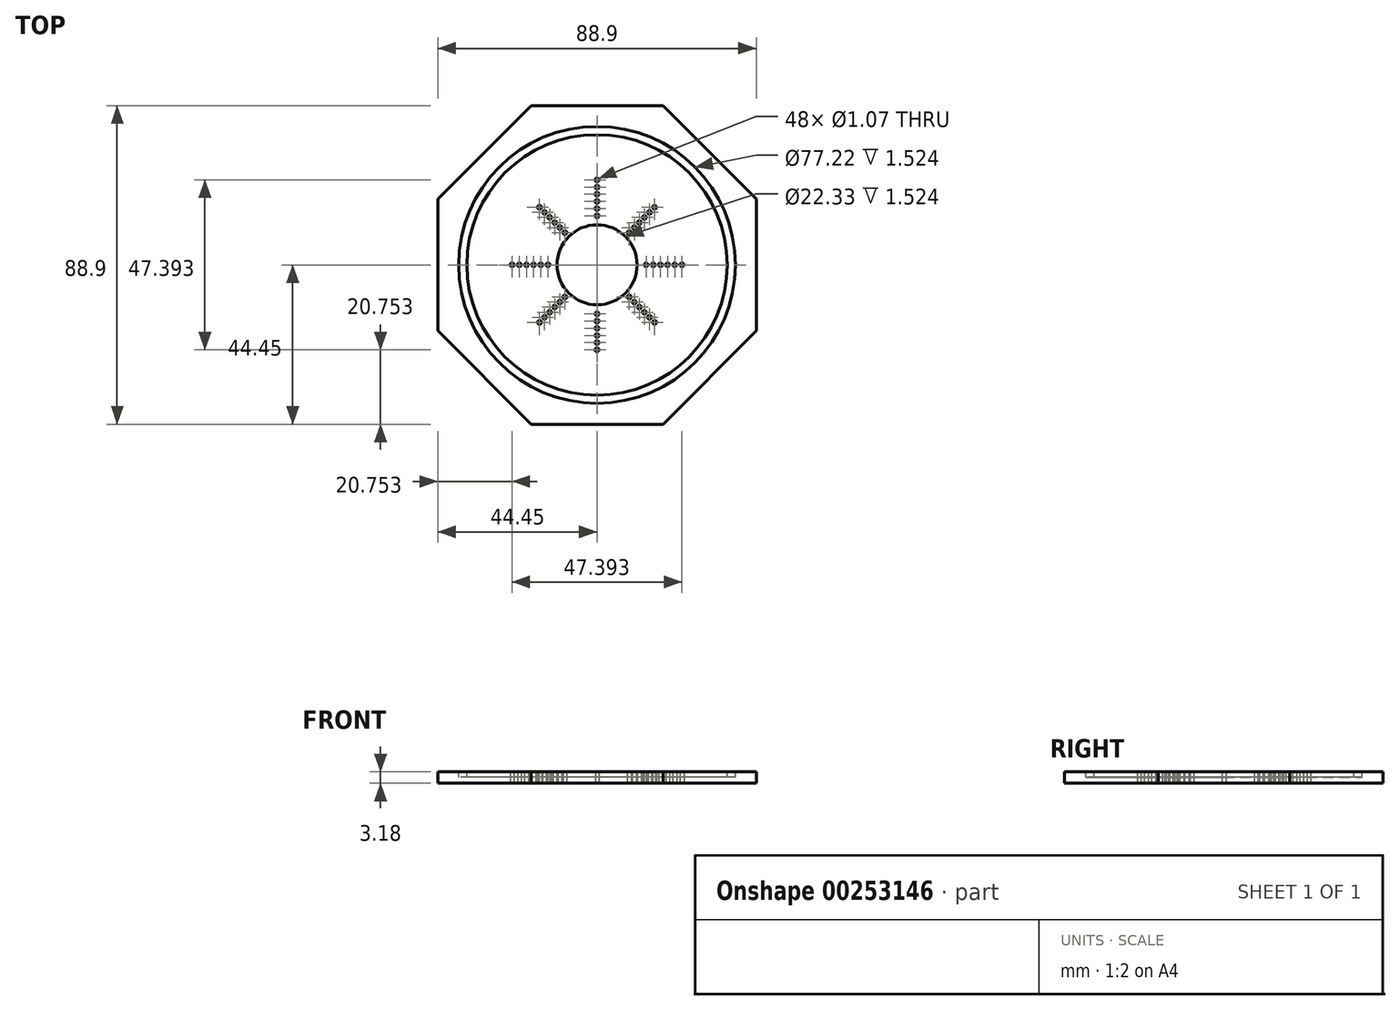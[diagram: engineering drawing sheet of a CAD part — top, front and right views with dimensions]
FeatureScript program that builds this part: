
annotation { "Feature Type Name" : "Feature", "Feature Type Description" : "" }
export const myFeature = defineFeature(function(context is Context, id is Id, definition is map)
    precondition{}
    {
        {
            var Q0;
            Q0=qCreatedBy(makeId("Top.planeOp"),FACE);
            var sketch = newSketch(context, id + "F0", { "sketchPlane" : qUnion([Q0])});
            skCircle(sketch, "E0", {"center": v(0, 0) * mm, "radius": 44.45 * mm, "construction": true});
            skLineSegment(sketch, "E1.bottom", {"start": v(-18.41, 44.45) * mm, "end": v(18.41, 44.45) * mm});
            skLineSegment(sketch, "E1.top", {"start": v(-18.41, -44.45) * mm, "end": v(18.41, -44.45) * mm});
            skLineSegment(sketch, "E1.left", {"start": v(-44.45, 18.41) * mm, "end": v(-44.45, -18.41) * mm});
            skLineSegment(sketch, "E1.right", {"start": v(44.45, 18.41) * mm, "end": v(44.45, -18.41) * mm});
            skLineSegment(sketch, "E2", {"start": v(-44.45, 18.41) * mm, "end": v(-18.41, 44.45) * mm});
            skLineSegment(sketch, "E3", {"start": v(0, 44.45) * mm, "end": v(0, -44.45) * mm, "construction": true});
            skLineSegment(sketch, "E4.MirrorCS", {"start": v(44.45, 18.41) * mm, "end": v(18.41, 44.45) * mm});
            skLineSegment(sketch, "E5", {"start": v(-44.45, 0) * mm, "end": v(44.45, 0) * mm});
            skLineSegment(sketch, "E6.MirrorCS", {"start": v(-44.45, -18.41) * mm, "end": v(-18.41, -44.45) * mm});
            skLineSegment(sketch, "E7.MirrorCS", {"start": v(44.45, -18.41) * mm, "end": v(18.41, -44.45) * mm});
            skPoint(sketch, "E8.orphan", {"position": v(-44.45, 44.45) * mm});
            skPoint(sketch, "E9.orphan", {"position": v(44.45, 44.45) * mm});
            skPoint(sketch, "E10.orphan", {"position": v(44.45, -44.45) * mm});
            skPoint(sketch, "E11.orphan", {"position": v(-44.45, -44.45) * mm});
            skSolve(sketch);
        }
        {
            var Q0;
            Q0=qSketchRegion(id+"F0",true);
            extrude(context, id + "F1", {"entities" : qUnion([Q0]), "depth" : 3.17 * mm});
        }
        {
            var Q0;
            Q0=makeQuery(id+"F1.opExtrude","CAP_FACE",FACE,{"disambiguationData":[OSD([sQuery(id+"F0.wireOp",EDGE,"E1.bottom"),sQuery(id+"F0.wireOp",EDGE,"E1.top"),sQuery(id+"F0.wireOp",EDGE,"E1.left"),sQuery(id+"F0.wireOp",EDGE,"E1.right")])],"isStart":false});
            var sketch = newSketch(context, id + "F2", { "sketchPlane" : qUnion([Q0])});
            skCircle(sketch, "E12", {"center": v(0, 0) * mm, "radius": 38.6 * mm});
            skCircle(sketch, "E13", {"center": v(0, 0) * mm, "radius": 36.32 * mm});
            skCircle(sketch, "E14", {"center": v(0, 0) * mm, "radius": 11.16 * mm});
            skSolve(sketch);
        }
        {
            var Q0;
            Q0=qSketchRegion(id+"F2",true);
            var Q1;
            Q1=makeQuery(id+"F2.imprint","IMPRINT",FACE,{"disambiguationData":[TD([[makeQuery(id+"F2.imprint","IMPRINT",EDGE,{"derivedFrom":sQuery(id+"F2.wireOp",EDGE,"E14")}),1.0]])]});
            extrude(context, id + "F3", {"entities" : qUnion([Q0, Q1]), "operationType" : NewBodyOperationType.REMOVE, "oppositeDirection" : true, "depth" : 1.52 * mm});
        }
        {
            var Q0;
            Q0=qCreatedBy(makeId("Top.planeOp"),FACE);
            var sketch = newSketch(context, id + "F4", { "sketchPlane" : qUnion([Q0])});
            skCircle(sketch, "E15", {"center": v(0, -13.7) * mm, "radius": 0.53 * mm});
            skCircle(sketch, "E16", {"center": v(0, -15.7) * mm, "radius": 0.53 * mm});
            skCircle(sketch, "E17", {"center": v(0, -17.7) * mm, "radius": 0.53 * mm});
            skCircle(sketch, "E18", {"center": v(0, -19.7) * mm, "radius": 0.53 * mm});
            skCircle(sketch, "E19", {"center": v(0, -21.7) * mm, "radius": 0.53 * mm});
            skCircle(sketch, "E20", {"center": v(0, -23.7) * mm, "radius": 0.53 * mm});
            skCircle(sketch, "E21.0", {"center": v(0, 0) * mm, "radius": 44.45 * mm, "construction": true});
            skLineSegment(sketch, "E22", {"start": v(31.43, 31.43) * mm, "end": v(-31.43, -31.43) * mm, "construction": true});
            skCircle(sketch, "E23", {"center": v(-8.98, -8.98) * mm, "radius": 0.53 * mm});
            skCircle(sketch, "E24", {"center": v(-10.4, -10.4) * mm, "radius": 0.53 * mm});
            skCircle(sketch, "E25", {"center": v(-11.8, -11.8) * mm, "radius": 0.53 * mm});
            skCircle(sketch, "E26", {"center": v(-13.22, -13.22) * mm, "radius": 0.53 * mm});
            skCircle(sketch, "E27", {"center": v(-14.63, -14.63) * mm, "radius": 0.53 * mm});
            skCircle(sketch, "E28", {"center": v(-16.05, -16.05) * mm, "radius": 0.53 * mm});
            skCircle(sketch, "E29.1.0", {"center": v(-21.7, 0) * mm, "radius": 0.53 * mm});
            skCircle(sketch, "E29.1.1", {"center": v(-23.7, 0) * mm, "radius": 0.53 * mm});
            skCircle(sketch, "E29.1.2", {"center": v(-13.7, 0) * mm, "radius": 0.53 * mm});
            skCircle(sketch, "E29.1.3", {"center": v(-17.7, 0) * mm, "radius": 0.53 * mm});
            skCircle(sketch, "E29.1.4", {"center": v(-15.7, 0) * mm, "radius": 0.53 * mm});
            skCircle(sketch, "E29.1.5", {"center": v(-19.7, 0) * mm, "radius": 0.53 * mm});
            skCircle(sketch, "E29.1.6", {"center": v(-16.05, 16.05) * mm, "radius": 0.53 * mm});
            skCircle(sketch, "E29.1.7", {"center": v(-14.63, 14.63) * mm, "radius": 0.53 * mm});
            skCircle(sketch, "E29.1.8", {"center": v(-8.98, 8.98) * mm, "radius": 0.53 * mm});
            skCircle(sketch, "E29.1.9", {"center": v(-10.4, 10.4) * mm, "radius": 0.53 * mm});
            skCircle(sketch, "E29.1.10", {"center": v(-13.22, 13.22) * mm, "radius": 0.53 * mm});
            skCircle(sketch, "E29.1.11", {"center": v(-11.8, 11.8) * mm, "radius": 0.53 * mm});
            skCircle(sketch, "E29.2.0", {"center": v(0, 21.7) * mm, "radius": 0.53 * mm});
            skCircle(sketch, "E29.2.1", {"center": v(0, 23.7) * mm, "radius": 0.53 * mm});
            skCircle(sketch, "E29.2.2", {"center": v(0, 13.7) * mm, "radius": 0.53 * mm});
            skCircle(sketch, "E29.2.3", {"center": v(0, 17.7) * mm, "radius": 0.53 * mm});
            skCircle(sketch, "E29.2.4", {"center": v(0, 15.7) * mm, "radius": 0.53 * mm});
            skCircle(sketch, "E29.2.5", {"center": v(0, 19.7) * mm, "radius": 0.53 * mm});
            skCircle(sketch, "E29.2.6", {"center": v(16.05, 16.05) * mm, "radius": 0.53 * mm});
            skCircle(sketch, "E29.2.7", {"center": v(14.63, 14.63) * mm, "radius": 0.53 * mm});
            skCircle(sketch, "E29.2.8", {"center": v(8.98, 8.98) * mm, "radius": 0.53 * mm});
            skCircle(sketch, "E29.2.9", {"center": v(10.4, 10.4) * mm, "radius": 0.53 * mm});
            skCircle(sketch, "E29.2.10", {"center": v(13.22, 13.22) * mm, "radius": 0.53 * mm});
            skCircle(sketch, "E29.2.11", {"center": v(11.8, 11.8) * mm, "radius": 0.53 * mm});
            skCircle(sketch, "E29.3.0", {"center": v(21.7, 0) * mm, "radius": 0.53 * mm});
            skCircle(sketch, "E29.3.1", {"center": v(23.7, 0) * mm, "radius": 0.53 * mm});
            skCircle(sketch, "E29.3.2", {"center": v(13.7, 0) * mm, "radius": 0.53 * mm});
            skCircle(sketch, "E29.3.3", {"center": v(17.7, 0) * mm, "radius": 0.53 * mm});
            skCircle(sketch, "E29.3.4", {"center": v(15.7, 0) * mm, "radius": 0.53 * mm});
            skCircle(sketch, "E29.3.5", {"center": v(19.7, 0) * mm, "radius": 0.53 * mm});
            skCircle(sketch, "E29.3.6", {"center": v(16.05, -16.05) * mm, "radius": 0.53 * mm});
            skCircle(sketch, "E29.3.7", {"center": v(14.63, -14.63) * mm, "radius": 0.53 * mm});
            skCircle(sketch, "E29.3.8", {"center": v(8.98, -8.98) * mm, "radius": 0.53 * mm});
            skCircle(sketch, "E29.3.9", {"center": v(10.4, -10.4) * mm, "radius": 0.53 * mm});
            skCircle(sketch, "E29.3.10", {"center": v(13.22, -13.22) * mm, "radius": 0.53 * mm});
            skCircle(sketch, "E29.3.11", {"center": v(11.8, -11.8) * mm, "radius": 0.53 * mm});
            skLineSegment(sketch, "E29.anchor1", {"start": v(0, 0) * mm, "end": v(-16.05, -16.05) * mm, "construction": true});
            skLineSegment(sketch, "E29.anchor2", {"start": v(0, 0) * mm, "end": v(16.05, -16.05) * mm, "construction": true});
            skSolve(sketch);
        }
        {
            var Q0;
            Q0=qSketchRegion(id+"F4",true);
            extrude(context, id + "F5", {"entities" : qUnion([Q0]), "operationType" : NewBodyOperationType.REMOVE, "endBound" : BoundingType.THROUGH_ALL, "depth" : 25.4 * mm});
        }
    });
